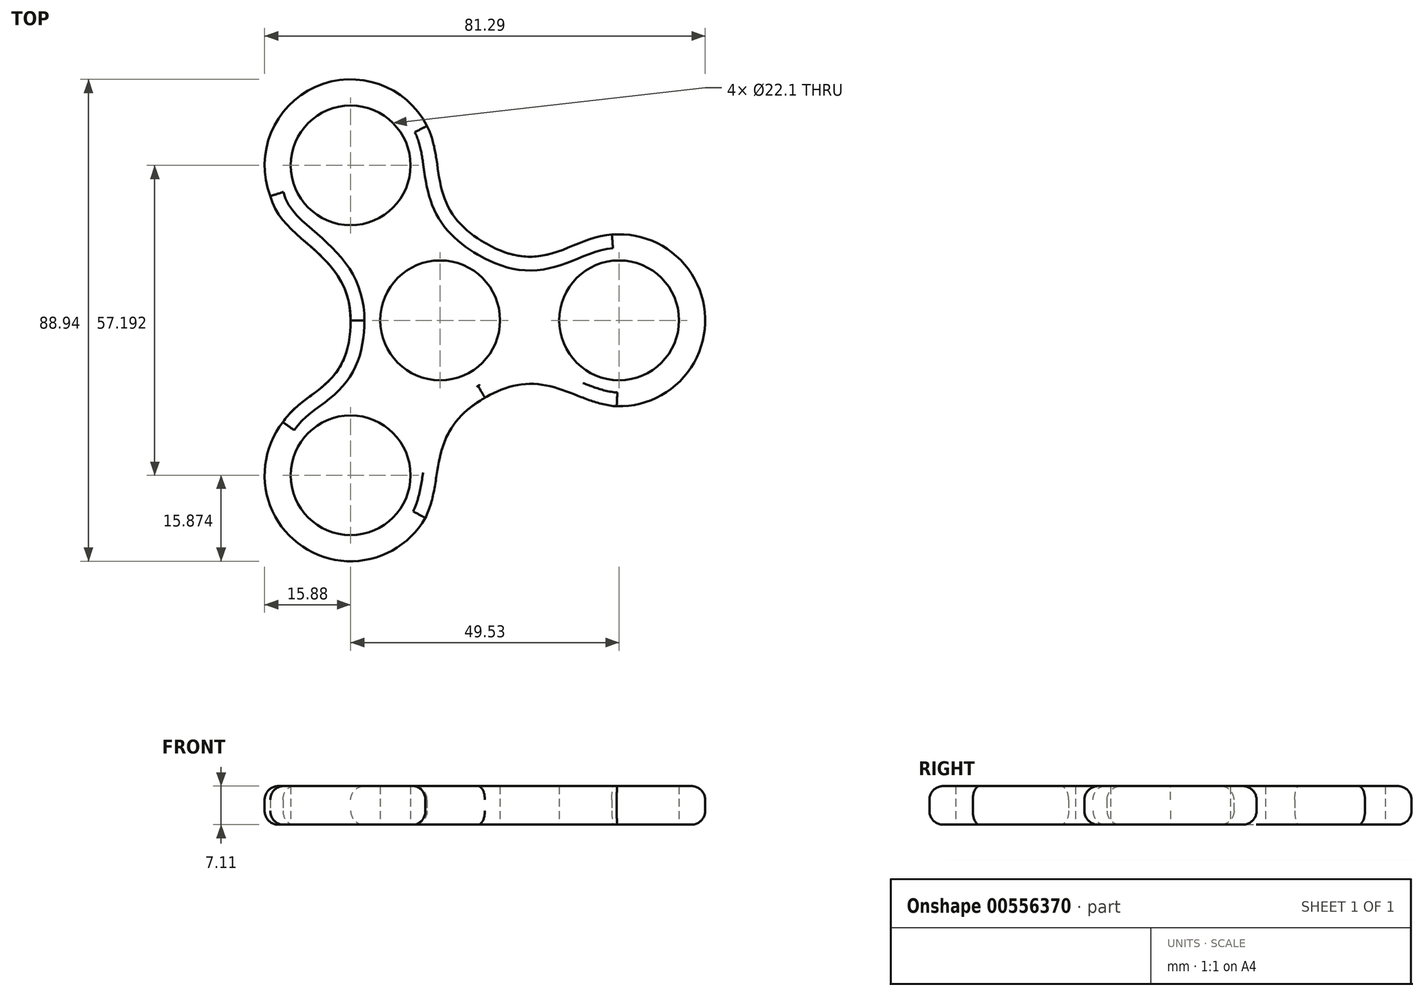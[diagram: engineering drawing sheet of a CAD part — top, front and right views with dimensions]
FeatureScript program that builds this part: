
annotation { "Feature Type Name" : "Feature", "Feature Type Description" : "" }
export const myFeature = defineFeature(function(context is Context, id is Id, definition is map)
    precondition{}
    {
        {
            var Q0;
            Q0=qCreatedBy(makeId("Top.planeOp"),FACE);
            var sketch = newSketch(context, id + "F0", { "sketchPlane" : qUnion([Q0])});
            skCircle(sketch, "E0.cCircle", {"center": v(0, 0) * mm, "radius": 16.51 * mm, "construction": true});
            skLineSegment(sketch, "E0.0", {"start": v(-16.51, -17.6) * mm, "end": v(-16.51, 17.6) * mm});
            skLineSegment(sketch, "E0.1", {"start": v(-6.99, 23.1) * mm, "end": v(23.5, 5.5) * mm});
            skLineSegment(sketch, "E0.2", {"start": v(23.5, -5.5) * mm, "end": v(-6.98, -23.1) * mm});
            skPoint(sketch, "E0.0.midPoint", {"position": v(-16.51, 0) * mm});
            skCircle(sketch, "E1", {"center": v(-16.51, 28.6) * mm, "radius": 11.05 * mm});
            skCircle(sketch, "E2", {"center": v(-16.51, 28.6) * mm, "radius": 15.88 * mm});
            skCircle(sketch, "E3", {"center": v(-16.51, -28.6) * mm, "radius": 11.05 * mm});
            skCircle(sketch, "E4", {"center": v(-16.51, -28.6) * mm, "radius": 15.88 * mm});
            skCircle(sketch, "E5", {"center": v(33.02, 0) * mm, "radius": 11.05 * mm});
            skCircle(sketch, "E6", {"center": v(33.02, 0) * mm, "radius": 15.88 * mm});
            skCircle(sketch, "E7", {"center": v(0, 0) * mm, "radius": 11.05 * mm});
            skArc(sketch, "E8.filletArc", {"start": v(-16.51, -17.6) * mm, "mid": v(-13.33, -23.1) * mm, "end": v(-6.98, -23.1) * mm});
            skArc(sketch, "E9.filletArc", {"start": v(23.5, -5.5) * mm, "mid": v(26.67, 0) * mm, "end": v(23.5, 5.5) * mm});
            skArc(sketch, "E10.filletArc", {"start": v(-6.99, 23.1) * mm, "mid": v(-13.34, 23.1) * mm, "end": v(-16.51, 17.6) * mm});
            skFitSpline(sketch, "E11", {"points": [v(8.26, -14.3) * mm, v(-2.72, -36.46) * mm], "startDerivative": vector(-32.94, -18.83) * mm, "endDerivative": vector(-10.97, -22.17) * mm});
            skFitSpline(sketch, "E12", {"points": [v(8.26, -14.3) * mm, v(32.58, -15.87) * mm], "startDerivative": vector(32.81, 19.2) * mm, "endDerivative": vector(24.32, -1.56) * mm});
            skFitSpline(sketch, "E13", {"points": [v(8.26, 14.3) * mm, v(31.69, 15.82) * mm], "startDerivative": vector(32.6, -19.03) * mm, "endDerivative": vector(23.43, 1.52) * mm});
            skFitSpline(sketch, "E14", {"points": [v(8.26, 14.3) * mm, v(-2.4, 35.88) * mm], "startDerivative": vector(-33.05, 19.08) * mm, "endDerivative": vector(-10.67, 21.57) * mm});
            skFitSpline(sketch, "E15", {"points": [v(-16.51, 0) * mm, v(-31.34, 22.92) * mm], "startDerivative": vector(-0.2, 37.62) * mm, "endDerivative": vector(-6.12, 25.4) * mm});
            skFitSpline(sketch, "E16", {"points": [v(-16.51, 0) * mm, v(-28.99, -18.78) * mm], "startDerivative": vector(-0.14, -38.18) * mm, "endDerivative": vector(-12.47, -18.8) * mm});
            skSolve(sketch);
        }
        {
            var Q0;
            {var subQ5=sQuery(id+"F0.wireOp",EDGE,"E3");var subQ7=sQuery(id+"F0.wireOp",EDGE,"E0.0");var subQ8=makeQuery(id+"F0.imprint","INTERSECT",VERTEX,{"derivedFrom":[subQ7,subQ5]});Q0=makeQuery(id+"F0.imprint","IMPRINT",FACE,{"disambiguationData":[TD([[makeQuery(id+"F0.imprint","IMPRINT",EDGE,{"disambiguationData":[TD([[subQ8,-1.0]])],"derivedFrom":subQ7}),1.0]])]});}
            var Q1;
            {var subQ1=sQuery(id+"F0.wireOp",EDGE,"E0.1");var subQ5=sQuery(id+"F0.wireOp",EDGE,"E6");var subQ8=makeQuery(id+"F0.imprint","INTERSECT",VERTEX,{"derivedFrom":[subQ1,subQ5]});Q1=makeQuery(id+"F0.imprint","IMPRINT",FACE,{"disambiguationData":[TD([[makeQuery(id+"F0.imprint","IMPRINT",EDGE,{"disambiguationData":[TD([[subQ8,-1.0]])],"derivedFrom":subQ1}),1.0]])]});}
            var Q2;
            {var subQ0=sQuery(id+"F0.wireOp",EDGE,"E6");var subQ1=sQuery(id+"F0.wireOp",EDGE,"E0.1");var subQ2=makeQuery(id+"F0.imprint","INTERSECT",VERTEX,{"derivedFrom":[subQ1,subQ0]});Q2=makeQuery(id+"F0.imprint","IMPRINT",FACE,{"disambiguationData":[TD([[makeQuery(id+"F0.imprint","IMPRINT",EDGE,{"disambiguationData":[TD([[subQ2,-1.0]])],"derivedFrom":subQ1}),-1.0]])]});}
            var Q3;
            {var subQ0=sQuery(id+"F0.wireOp",EDGE,"E3");var subQ1=sQuery(id+"F0.wireOp",EDGE,"E0.0");var subQ2=makeQuery(id+"F0.imprint","INTERSECT",VERTEX,{"derivedFrom":[subQ1,subQ0]});Q3=makeQuery(id+"F0.imprint","IMPRINT",FACE,{"disambiguationData":[TD([[makeQuery(id+"F0.imprint","IMPRINT",EDGE,{"disambiguationData":[TD([[subQ2,-1.0]])],"derivedFrom":subQ1}),-1.0]])]});}
            var Q4;
            Q4=makeQuery(id+"F0.imprint","IMPRINT",FACE,{"disambiguationData":[TD([[makeQuery(id+"F0.imprint","IMPRINT",EDGE,{"derivedFrom":sQuery(id+"F0.wireOp",EDGE,"E7")}),-1.0]])]});
            var Q5;
            {var subQ1=sQuery(id+"F0.wireOp",EDGE,"E0.0");var subQ6=sQuery(id+"F0.wireOp",EDGE,"E2");var subQ11=makeQuery(id+"F0.imprint","INTERSECT",VERTEX,{"derivedFrom":[subQ1,subQ6]});Q5=makeQuery(id+"F0.imprint","IMPRINT",FACE,{"disambiguationData":[TD([[makeQuery(id+"F0.imprint","IMPRINT",EDGE,{"disambiguationData":[TD([[subQ11,-1.0]])],"derivedFrom":subQ1}),1.0]])]});}
            var Q6;
            {var subQ0=sQuery(id+"F0.wireOp",EDGE,"E2");var subQ1=sQuery(id+"F0.wireOp",EDGE,"E0.0");var subQ2=makeQuery(id+"F0.imprint","INTERSECT",VERTEX,{"derivedFrom":[subQ1,subQ0]});Q6=makeQuery(id+"F0.imprint","IMPRINT",FACE,{"disambiguationData":[TD([[makeQuery(id+"F0.imprint","IMPRINT",EDGE,{"disambiguationData":[TD([[subQ2,-1.0]])],"derivedFrom":subQ1}),-1.0]])]});}
            var Q7;
            {var subQ0=sQuery(id+"F0.wireOp",EDGE,"E11");var subQ1=sQuery(id+"F0.wireOp",EDGE,"E0.2");var subQ2=makeQuery(id+"F0.imprint","INTERSECT",VERTEX,{"derivedFrom":[subQ1,subQ0]});Q7=makeQuery(id+"F0.imprint","IMPRINT",FACE,{"disambiguationData":[TD([[makeQuery(id+"F0.imprint","IMPRINT",EDGE,{"disambiguationData":[TD([[subQ2,-1.0]])],"derivedFrom":subQ1}),1.0]])]});}
            var Q8;
            {var subQ0=sQuery(id+"F0.wireOp",EDGE,"E12");var subQ1=sQuery(id+"F0.wireOp",EDGE,"E0.2");var subQ2=makeQuery(id+"F0.imprint","INTERSECT",VERTEX,{"derivedFrom":[subQ1,subQ0]});Q8=makeQuery(id+"F0.imprint","IMPRINT",FACE,{"disambiguationData":[TD([[makeQuery(id+"F0.imprint","IMPRINT",EDGE,{"disambiguationData":[TD([[subQ2,1.0]])],"derivedFrom":subQ1}),1.0]])]});}
            var Q9;
            {var subQ0=sQuery(id+"F0.wireOp",EDGE,"E13");var subQ1=sQuery(id+"F0.wireOp",EDGE,"E0.1");var subQ2=makeQuery(id+"F0.imprint","INTERSECT",VERTEX,{"derivedFrom":[subQ1,subQ0]});Q9=makeQuery(id+"F0.imprint","IMPRINT",FACE,{"disambiguationData":[TD([[makeQuery(id+"F0.imprint","IMPRINT",EDGE,{"disambiguationData":[TD([[subQ2,-1.0]])],"derivedFrom":subQ1}),1.0]])]});}
            var Q10;
            {var subQ0=sQuery(id+"F0.wireOp",EDGE,"E14");var subQ3=sQuery(id+"F0.wireOp",EDGE,"E2");var subQ5=makeQuery(id+"F0.imprint","INTERSECT",VERTEX,{"disambiguationData":[OD(1.0)],"derivedFrom":[subQ3,subQ0]});Q10=makeQuery(id+"F0.imprint","IMPRINT",FACE,{"disambiguationData":[TD([[makeQuery(id+"F0.imprint","IMPRINT",EDGE,{"disambiguationData":[TD([[subQ5,1.0]])],"derivedFrom":subQ3}),-1.0]])]});}
            var Q11;
            {var subQ0=sQuery(id+"F0.wireOp",EDGE,"E15");Q11=makeQuery(id+"F0.imprint","IMPRINT",FACE,{"disambiguationData":[TD([[makeQuery(id+"F0.imprint","IMPRINT",EDGE,{"derivedFrom":subQ0}),-1.0]])]});}
            var Q12;
            {var subQ0=sQuery(id+"F0.wireOp",EDGE,"E16");Q12=makeQuery(id+"F0.imprint","IMPRINT",FACE,{"disambiguationData":[TD([[makeQuery(id+"F0.imprint","IMPRINT",EDGE,{"derivedFrom":subQ0}),1.0]])]});}
            extrude(context, id + "F1", {"entities" : qUnion([Q0, Q1, Q2, Q3, Q4, Q5, Q6, Q7, Q8, Q9, Q10, Q11, Q12]), "depth" : 7.11 * mm, "offsetDistance" : 25.4 * mm});
        }
        {
            var Q0;
            Q0=makeQuery(id+"F1.opExtrude","CAP_EDGE",EDGE,{"disambiguationData":[OSD([sQuery(id+"F0.wireOp",EDGE,"E6")])],"isStart":false});
            var Q1;
            Q1=makeQuery(id+"F1.opExtrude","CAP_EDGE",EDGE,{"disambiguationData":[OSD([sQuery(id+"F0.wireOp",EDGE,"E12")])],"isStart":false});
            var Q2;
            Q2=makeQuery(id+"F1.opExtrude","CAP_EDGE",EDGE,{"disambiguationData":[OSD([sQuery(id+"F0.wireOp",EDGE,"E13")])],"isStart":false});
            var Q3;
            Q3=makeQuery(id+"F1.opExtrude","CAP_EDGE",EDGE,{"disambiguationData":[OSD([sQuery(id+"F0.wireOp",EDGE,"E11")])],"isStart":false});
            var Q4;
            Q4=makeQuery(id+"F1.opExtrude","CAP_EDGE",EDGE,{"disambiguationData":[OSD([sQuery(id+"F0.wireOp",EDGE,"E4")])],"isStart":false});
            var Q5;
            Q5=makeQuery(id+"F1.opExtrude","CAP_EDGE",EDGE,{"disambiguationData":[OSD([sQuery(id+"F0.wireOp",EDGE,"E16")])],"isStart":false});
            var Q6;
            Q6=makeQuery(id+"F1.opExtrude","CAP_EDGE",EDGE,{"disambiguationData":[OSD([sQuery(id+"F0.wireOp",EDGE,"E15")])],"isStart":false});
            var Q7;
            Q7=makeQuery(id+"F1.opExtrude","CAP_EDGE",EDGE,{"disambiguationData":[OSD([sQuery(id+"F0.wireOp",EDGE,"E2")])],"isStart":false});
            var Q8;
            Q8=makeQuery(id+"F1.opExtrude","CAP_EDGE",EDGE,{"disambiguationData":[OSD([sQuery(id+"F0.wireOp",EDGE,"E14")])],"isStart":false});
            var Q9;
            Q9=makeQuery(id+"F1.opExtrude","CAP_EDGE",EDGE,{"disambiguationData":[OSD([sQuery(id+"F0.wireOp",EDGE,"E2")])],"isStart":true});
            var Q10;
            Q10=makeQuery(id+"F1.opExtrude","CAP_EDGE",EDGE,{"disambiguationData":[OSD([sQuery(id+"F0.wireOp",EDGE,"E14")])],"isStart":true});
            var Q11;
            Q11=makeQuery(id+"F1.opExtrude","CAP_EDGE",EDGE,{"disambiguationData":[OSD([sQuery(id+"F0.wireOp",EDGE,"E13")])],"isStart":true});
            var Q12;
            Q12=makeQuery(id+"F1.opExtrude","CAP_EDGE",EDGE,{"disambiguationData":[OSD([sQuery(id+"F0.wireOp",EDGE,"E6")])],"isStart":true});
            var Q13;
            Q13=makeQuery(id+"F1.opExtrude","CAP_EDGE",EDGE,{"disambiguationData":[OSD([sQuery(id+"F0.wireOp",EDGE,"E12")])],"isStart":true});
            var Q14;
            Q14=makeQuery(id+"F1.opExtrude","CAP_EDGE",EDGE,{"disambiguationData":[OSD([sQuery(id+"F0.wireOp",EDGE,"E11")])],"isStart":true});
            var Q15;
            Q15=makeQuery(id+"F1.opExtrude","CAP_EDGE",EDGE,{"disambiguationData":[OSD([sQuery(id+"F0.wireOp",EDGE,"E4")])],"isStart":true});
            var Q16;
            Q16=makeQuery(id+"F1.opExtrude","CAP_EDGE",EDGE,{"disambiguationData":[OSD([sQuery(id+"F0.wireOp",EDGE,"E16")])],"isStart":true});
            var Q17;
            Q17=makeQuery(id+"F1.opExtrude","CAP_EDGE",EDGE,{"disambiguationData":[OSD([sQuery(id+"F0.wireOp",EDGE,"E15")])],"isStart":true});
            fillet(context, id + "F2", {"entities" : qUnion([Q0, Q1, Q2, Q3, Q4, Q5, Q6, Q7, Q8, Q9, Q10, Q11, Q12, Q13, Q14, Q15, Q16, Q17]), "radius" : 2.54 * mm, "tangentPropagation" : true, "allowEdgeOverflow" : false});
        }
    });
